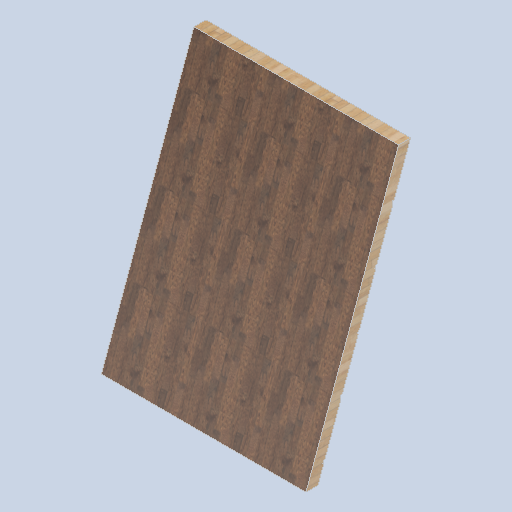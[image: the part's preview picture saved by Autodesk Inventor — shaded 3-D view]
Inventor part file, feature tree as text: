
AUTODESK INVENTOR PART (.ipt)
format: ipt  version: 2024.2 (Build 282272000, 272)  size: 294,400 bytes
history: native  units: in
note: dims shown in document units (in); Inventor stores cm internally (conversion verified against a paired STEP export)
features: other x3, sketch x2
ambient origin geometry x8: Origin, YZ Plane, XZ Plane, XY Plane, X Axis, Y Axis, Z Axis, Center Point
bodies: Solid1 (feature_tree)
feature tree (5):
  other  "side_curve_panel_02.ipt"
  other  "Solid1::side_curve_panel_02.ipt"
  other  "TaggingFeature1"
  sketch  "Sketch1"  dims[d0=0.3937in]
  sketch  "Sketch2"
